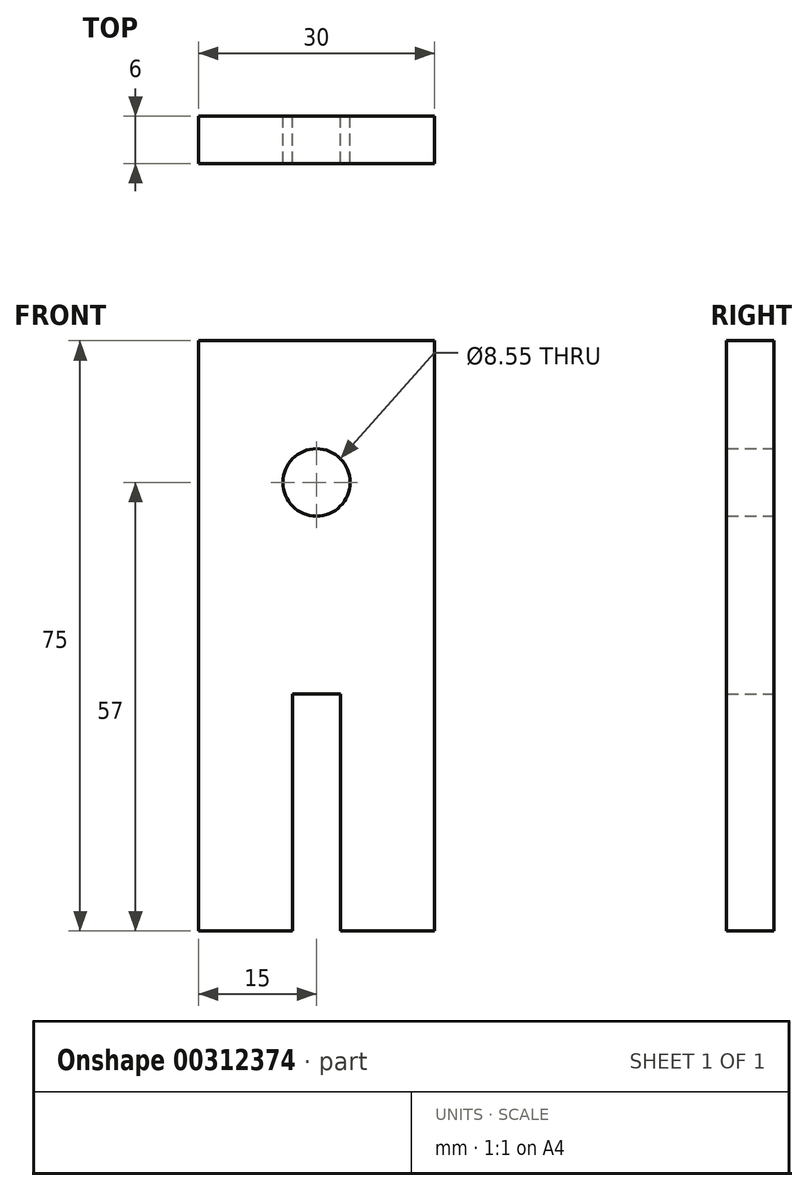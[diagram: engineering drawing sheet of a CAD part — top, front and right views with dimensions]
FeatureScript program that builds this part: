
annotation { "Feature Type Name" : "Feature", "Feature Type Description" : "" }
export const myFeature = defineFeature(function(context is Context, id is Id, definition is map)
    precondition{}
    {
        {
            var Q0;
            Q0=qCreatedBy(makeId("Front.planeOp"),FACE);
            var sketch = newSketch(context, id + "F0", { "sketchPlane" : qUnion([Q0])});
            skLineSegment(sketch, "E0", {"start": v(0, 0) * mm, "end": v(0, 0) * mm});
            skLineSegment(sketch, "E1", {"start": v(0, 0) * mm, "end": v(0, -75) * mm});
            skLineSegment(sketch, "E2", {"start": v(0, -75) * mm, "end": v(11.95, -75) * mm});
            skLineSegment(sketch, "E3", {"start": v(11.95, -75) * mm, "end": v(11.95, -44.9) * mm});
            skLineSegment(sketch, "E4", {"start": v(11.95, -44.9) * mm, "end": v(18.05, -44.9) * mm});
            skLineSegment(sketch, "E5", {"start": v(18.05, -44.9) * mm, "end": v(18.05, -75) * mm});
            skLineSegment(sketch, "E6", {"start": v(18.05, -75) * mm, "end": v(30, -75) * mm});
            skLineSegment(sketch, "E7", {"start": v(30, -75) * mm, "end": v(30, 0) * mm});
            skLineSegment(sketch, "E8", {"start": v(30, 0) * mm, "end": v(0, 0) * mm});
            skCircle(sketch, "E9", {"center": v(15, -18) * mm, "radius": 4.28 * mm});
            skPoint(sketch, "E9.centerSnap0", {"position": v(15, 0) * mm});
            skPoint(sketch, "E10", {"position": v(15, -44.9) * mm});
            skSolve(sketch);
        }
        {
            var Q0;
            Q0=makeQuery(id+"F0.imprint","IMPRINT",FACE,{"disambiguationData":[TD([[makeQuery(id+"F0.imprint","IMPRINT",EDGE,{"derivedFrom":sQuery(id+"F0.wireOp",EDGE,"E1")}),1.0]])]});
            extrude(context, id + "F1", {"entities" : qUnion([Q0]), "depth" : 6 * mm});
        }
    });
